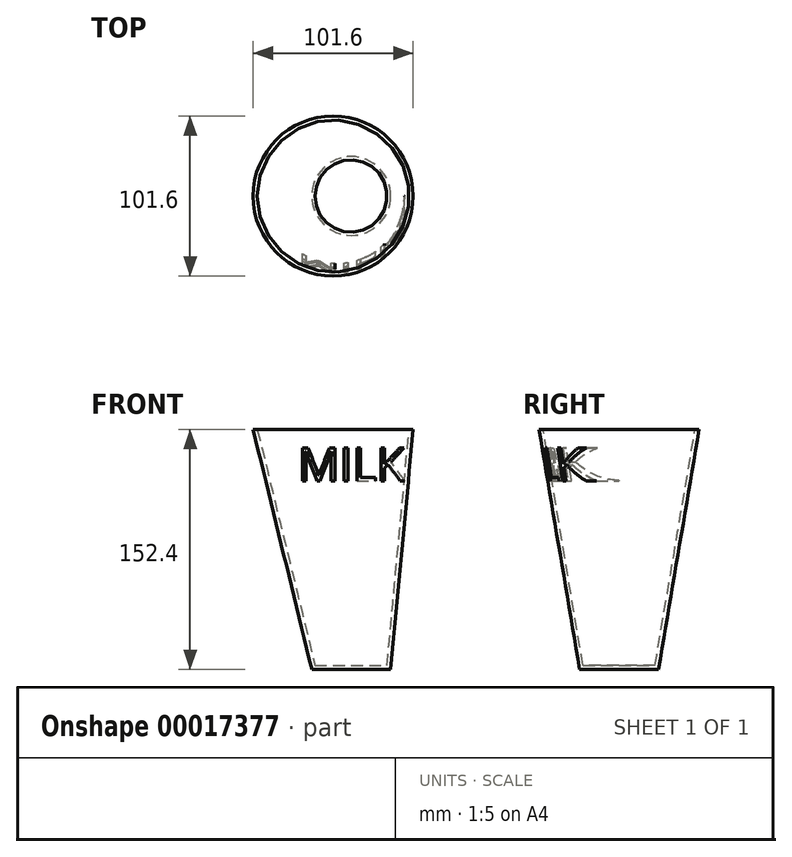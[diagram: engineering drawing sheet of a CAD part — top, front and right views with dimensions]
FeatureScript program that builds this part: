
annotation { "Feature Type Name" : "Feature", "Feature Type Description" : "" }
export const myFeature = defineFeature(function(context is Context, id is Id, definition is map)
    precondition{}
    {
        {
            var Q0;
            Q0=qCreatedBy(makeId("Top.planeOp"),FACE);
            var sketch = newSketch(context, id + "F0", { "sketchPlane" : qUnion([Q0])});
            skCircle(sketch, "E0", {"center": v(0, 0) * mm, "radius": 25.06 * mm});
            skSolve(sketch);
        }
        {
            var Q0;
            Q0=qCreatedBy(makeId("Top.planeOp"),FACE);
            cPlane(context, id + "F1", {"entities" : qUnion([Q0]), "cplaneType" : CPlaneType.OFFSET, "offset" : 152.4 * mm, "width" : 152.4 * mm, "height" : 152.4 * mm});
        }
        {
            var Q0;
            Q0=qCreatedBy(id+"F1.planeOp",FACE);
            var sketch = newSketch(context, id + "F2", { "sketchPlane" : qUnion([Q0])});
            skCircle(sketch, "E1", {"center": v(-11.51, 0) * mm, "radius": 50.8 * mm});
            skSolve(sketch);
        }
        {
            var Q0;
            Q0=makeQuery(id+"F2.imprint","IMPRINT",FACE,{"disambiguationData":[TD([[makeQuery(id+"F2.imprint","IMPRINT",EDGE,{"derivedFrom":sQuery(id+"F2.wireOp",EDGE,"E1")}),1.0]])]});
            var Q1;
            Q1=makeQuery(id+"F0.imprint","IMPRINT",FACE,{"disambiguationData":[TD([[makeQuery(id+"F0.imprint","IMPRINT",EDGE,{"derivedFrom":sQuery(id+"F0.wireOp",EDGE,"E0")}),1.0]])]});
            loft(context, id + "F3", {"sheetProfilesArray" : [{ "sheetProfileEntities" : qUnion([Q0]) }, { "sheetProfileEntities" : qUnion([Q1]) }]});
        }
        {
            var Q0;
            Q0=makeQuery(id+"F3.opLoft","CAP_FACE",FACE,{"disambiguationData":[OSD([makeQuery(id+"F2.imprint","IMPRINT",FACE,{"disambiguationData":[TD([[makeQuery(id+"F2.imprint","IMPRINT",EDGE,{"derivedFrom":sQuery(id+"F2.wireOp",EDGE,"E1")}),1.0]])]})])],"isStart":true});
            shell(context, id + "F4", {"entities" : qUnion([Q0]), "thickness" : 2.54 * mm});
        }
        {
            var Q0;
            Q0=qCreatedBy(makeId("Front.planeOp"),FACE);
            var sketch = newSketch(context, id + "F5", { "sketchPlane" : qUnion([Q0])});
            skText(sketch, "E2", { "text": "MILK", "fontName": "OpenSans-Regular.ttf"});
            const initialGuessF5  = {"E2": [-0.03389, 0.11987, 1, 0, 0.02109]};
            skSetInitialGuess(sketch, initialGuessF5);
            skSolve(sketch);
        }
        {
            var Q0;
            Q0 = qSketchRegion(id + "F5", true);
            extrude(context, id + "F6", {"entities" : qUnion([Q0]), "operationType" : NewBodyOperationType.INTERSECT, "depth" : 76.2 * mm});
        }
        {
            var Q0;
            Q0=makeQuery(id+"F2.imprint","IMPRINT",FACE,{"disambiguationData":[TD([[makeQuery(id+"F2.imprint","IMPRINT",EDGE,{"derivedFrom":sQuery(id+"F2.wireOp",EDGE,"E1")}),1.0]])]});
            var Q1;
            Q1=makeQuery(id+"F0.imprint","IMPRINT",FACE,{"disambiguationData":[TD([[makeQuery(id+"F0.imprint","IMPRINT",EDGE,{"derivedFrom":sQuery(id+"F0.wireOp",EDGE,"E0")}),1.0]])]});
            loft(context, id + "F7", {"sheetProfilesArray" : [{ "sheetProfileEntities" : qUnion([Q0]) }, { "sheetProfileEntities" : qUnion([Q1]) }]});
        }
        {
            var Q0;
            Q0=makeQuery(id+"F7.opLoft","CAP_FACE",FACE,{"disambiguationData":[OSD([makeQuery(id+"F2.imprint","IMPRINT",FACE,{"disambiguationData":[TD([[makeQuery(id+"F2.imprint","IMPRINT",EDGE,{"derivedFrom":sQuery(id+"F2.wireOp",EDGE,"E1")}),1.0]])]})])],"isStart":true});
            shell(context, id + "F8", {"entities" : qUnion([Q0]), "thickness" : 2.54 * mm});
        }
        {
            var Q0;
            Q0=qCreatedBy(makeId("Front.planeOp"),FACE);
            var sketch = newSketch(context, id + "F9", { "sketchPlane" : qUnion([Q0])});
            skFitSpline(sketch, "E3", {"points": [v(-55.33, 133.56) * mm, v(-81.73, 121.9) * mm, v(-53.7, 36.97) * mm, v(-28.93, 31.65) * mm, v(-28.52, 32.06) * mm], "startDerivative": vector(-128.76, -5.37) * mm, "endDerivative": vector(4.77, 10.56) * mm});
            skSolve(sketch);
        }
        {
            var Q0;
            Q0=qCreatedBy(makeId("Right.planeOp"),FACE);
            cPlane(context, id + "F10", {"entities" : qUnion([Q0]), "cplaneType" : CPlaneType.OFFSET, "offset" : 50.8 * mm, "oppositeDirection" : true, "width" : 152.4 * mm, "height" : 152.4 * mm});
        }
        {
            var Q0;
            Q0=qCreatedBy(id+"F10.planeOp",FACE);
            var sketch = newSketch(context, id + "F11", { "sketchPlane" : qUnion([Q0])});
            skLineSegment(sketch, "E4.rect.bottom", {"start": v(-8.2, 135.6) * mm, "end": v(8.2, 135.6) * mm});
            skLineSegment(sketch, "E4.rect.top", {"start": v(-8.2, 142.8) * mm, "end": v(8.2, 142.8) * mm});
            skLineSegment(sketch, "E4.rect.left", {"start": v(-8.2, 135.6) * mm, "end": v(-8.2, 142.8) * mm});
            skLineSegment(sketch, "E4.rect.right", {"start": v(8.2, 135.6) * mm, "end": v(8.2, 142.8) * mm});
            skPoint(sketch, "E4.rect.middle", {"position": v(0, 139.2) * mm});
            skSolve(sketch);
        }
    });
